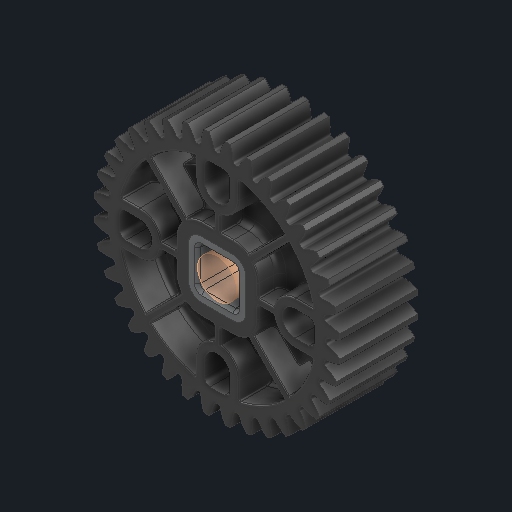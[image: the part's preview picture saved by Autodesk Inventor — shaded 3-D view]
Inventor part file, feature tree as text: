
AUTODESK INVENTOR PART (.ipt)
format: ipt  version: 2025 (Build 290162000, 162)  size: 3,317,760 bytes
history: native  units: in
note: dims shown in document units (in); Inventor stores cm internally (conversion verified against a paired STEP export)
features: other x6, sketch x1
ambient origin geometry x8: Origin, YZ Plane, XZ Plane, XY Plane, X Axis, Y Axis, Z Axis, Center Point
bodies: Solid1 (feature_tree), Solid2 (feature_tree)
feature tree (7):
  other  "HS 36T Gear, No Insert.ipt"
  other  "Solid1::HS 36T Gear, No Insert.ipt"
  other  "Solid2::HS 36T Gear, No Insert.ipt"
  other  "TaggingFeature1"
  sketch  "Sketch1"  dims[d0=0.3937in]
  other  "Srf1"
  other  "Srf1::Derived"
